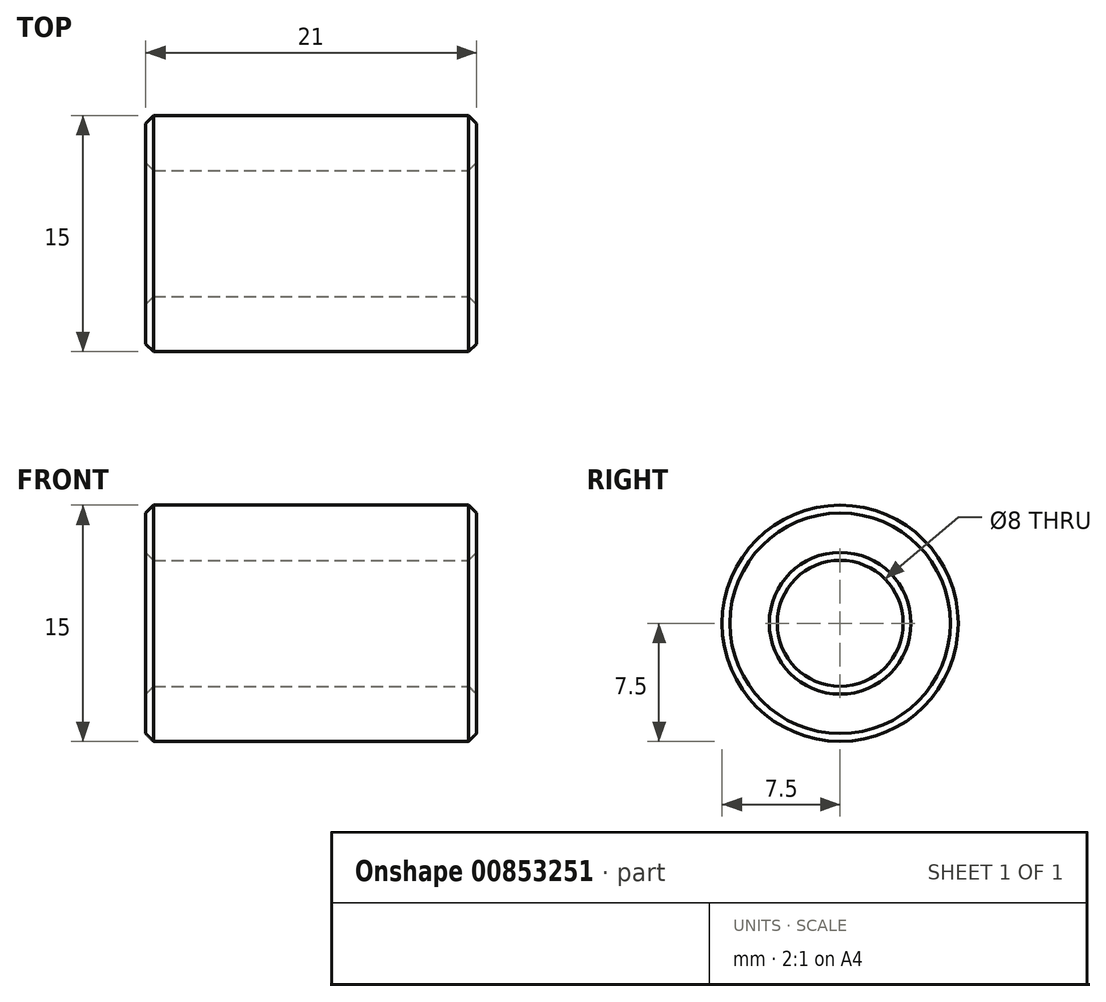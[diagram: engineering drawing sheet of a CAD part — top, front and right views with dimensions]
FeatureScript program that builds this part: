
annotation { "Feature Type Name" : "Feature", "Feature Type Description" : "" }
export const myFeature = defineFeature(function(context is Context, id is Id, definition is map)
    precondition{}
    {
        {
            var Q0;
            Q0=qCreatedBy(makeId("Front.planeOp"),FACE);
            var sketch = newSketch(context, id + "F0", { "sketchPlane" : qUnion([Q0])});
            skLineSegment(sketch, "E0.bottom", {"start": v(-10.5, 4) * mm, "end": v(10.5, 4) * mm});
            skLineSegment(sketch, "E0.top", {"start": v(-10.5, 7.5) * mm, "end": v(10.5, 7.5) * mm});
            skLineSegment(sketch, "E0.left", {"start": v(-10.5, 4) * mm, "end": v(-10.5, 7.5) * mm});
            skLineSegment(sketch, "E0.right", {"start": v(10.5, 4) * mm, "end": v(10.5, 7.5) * mm});
            skLineSegment(sketch, "E1", {"start": v(16.1, 0) * mm, "end": v(-16.94, 0) * mm, "construction": true});
            skSolve(sketch);
        }
        {
            var Q0;
            Q0=makeQuery(id+"F0.imprint","IMPRINT",FACE,{"disambiguationData":[TD([[makeQuery(id+"F0.imprint","IMPRINT",EDGE,{"derivedFrom":sQuery(id+"F0.wireOp",EDGE,"E0.bottom")}),1.0]])]});
            var Q1;
            Q1=sQuery(id+"F0.wireOp",EDGE,"E0.top");
            var Q2;
            Q2=sQuery(id+"F0.wireOp",EDGE,"E0.left");
            var Q3;
            Q3=sQuery(id+"F0.wireOp",EDGE,"E0.bottom");
            var Q4;
            Q4=sQuery(id+"F0.wireOp",EDGE,"E0.right");
            var Q5;
            Q5=sQuery(id+"F0.wireOp",EDGE,"E1");
            revolve(context, id + "F1", {"surfaceOperationType" : NewSurfaceOperationType.NEW, "entities" : qUnion([Q0]), "surfaceEntities" : qUnion([Q1, Q2, Q3, Q4]), "axis" : qUnion([Q5]), "revolveType" : RevolveType.FULL});
        }
        {
            var Q0;
            Q0=makeQuery(id+"F1.opRevolve","SWEPT_EDGE",EDGE,{"disambiguationData":[OSD([sQuery(id+"F0.wireOp",EDGE,"E0.top"),sQuery(id+"F0.wireOp",EDGE,"E0.right")])]});
            var Q1;
            Q1=makeQuery(id+"F1.opRevolve","SWEPT_EDGE",EDGE,{"disambiguationData":[OSD([sQuery(id+"F0.wireOp",EDGE,"E0.bottom"),sQuery(id+"F0.wireOp",EDGE,"E0.right")])]});
            var Q2;
            Q2=makeQuery(id+"F1.opRevolve","SWEPT_EDGE",EDGE,{"disambiguationData":[OSD([sQuery(id+"F0.wireOp",EDGE,"E0.bottom"),sQuery(id+"F0.wireOp",EDGE,"E0.left")])]});
            var Q3;
            Q3=makeQuery(id+"F1.opRevolve","SWEPT_EDGE",EDGE,{"disambiguationData":[OSD([sQuery(id+"F0.wireOp",EDGE,"E0.top"),sQuery(id+"F0.wireOp",EDGE,"E0.left")])]});
            chamfer(context, id + "F2", {"entities" : qUnion([Q0, Q1, Q2, Q3]), "width" : 0.5 * mm, "tangentPropagation" : true});
        }
    });
